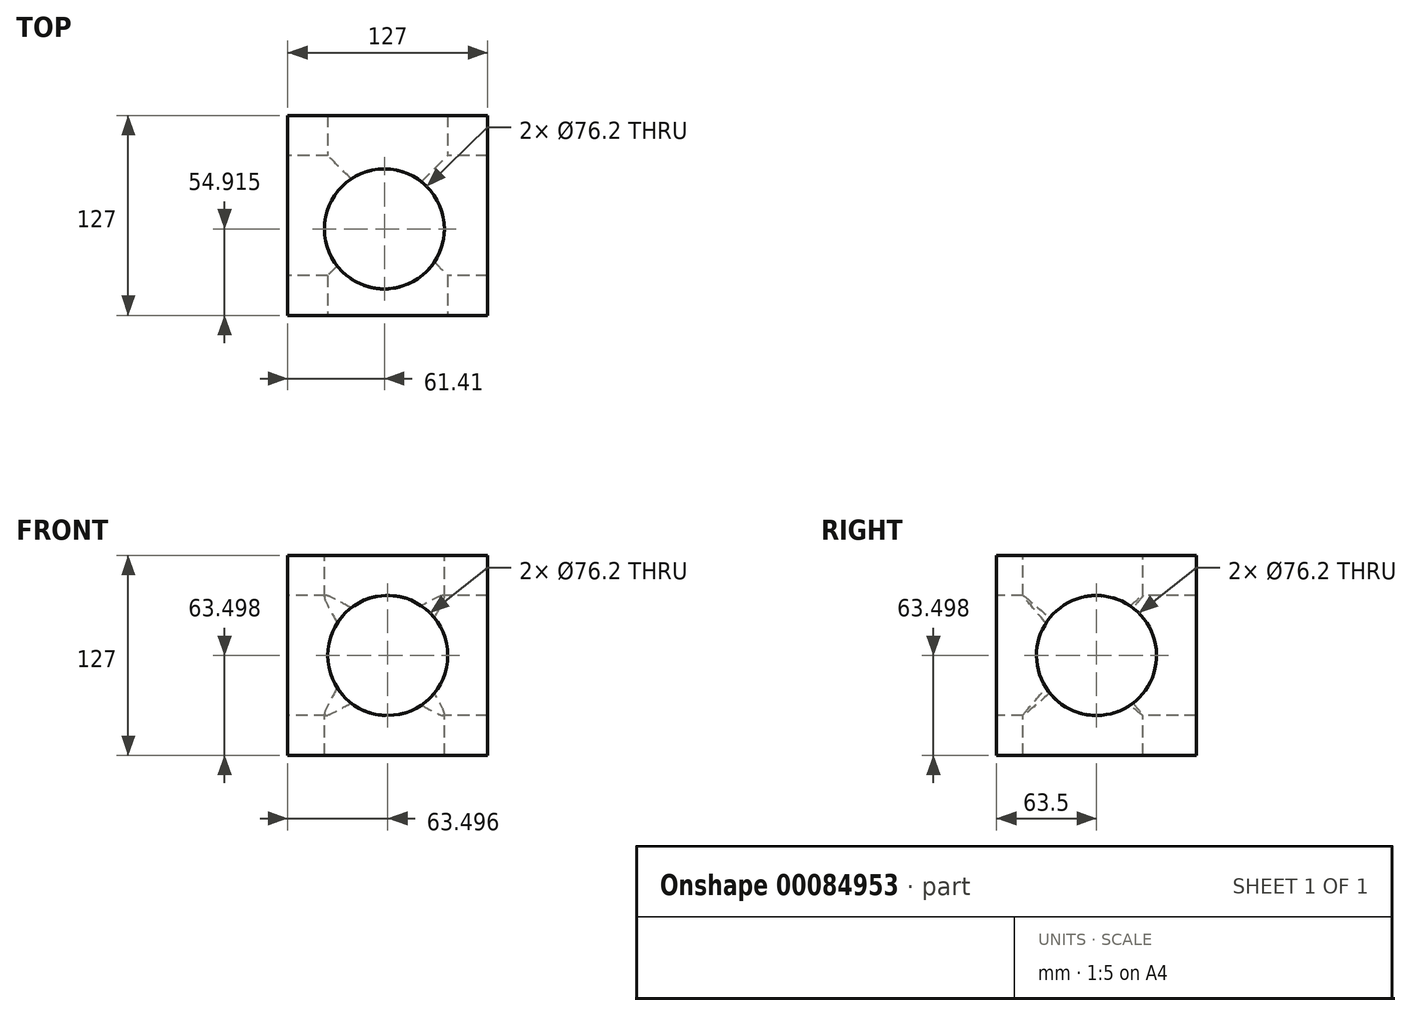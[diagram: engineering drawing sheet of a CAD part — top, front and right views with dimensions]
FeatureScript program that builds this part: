
annotation { "Feature Type Name" : "Feature", "Feature Type Description" : "" }
export const myFeature = defineFeature(function(context is Context, id is Id, definition is map)
    precondition{}
    {
        {
            var Q0;
            Q0=qCreatedBy(makeId("Front.planeOp"),FACE);
            var sketch = newSketch(context, id + "F0", { "sketchPlane" : qUnion([Q0])});
            skLineSegment(sketch, "E0.bottom", {"start": v(-61.41, 52.56) * mm, "end": v(65.59, 52.56) * mm});
            skLineSegment(sketch, "E0.top", {"start": v(-61.41, -74.44) * mm, "end": v(65.59, -74.44) * mm});
            skLineSegment(sketch, "E0.left", {"start": v(-61.41, 52.56) * mm, "end": v(-61.41, -74.44) * mm});
            skLineSegment(sketch, "E0.right", {"start": v(65.59, 52.56) * mm, "end": v(65.59, -74.44) * mm});
            skSolve(sketch);
        }
        {
            var Q0;
            Q0 = qSketchRegion(id + "F0", true);
            extrude(context, id + "F1", {"entities" : qUnion([Q0]), "depth" : 127 * mm});
        }
        {
            var Q0;
            Q0=makeQuery(id+"F1.opExtrude","CAP_FACE",FACE,{"disambiguationData":[OSD([sQuery(id+"F0.wireOp",EDGE,"E0.bottom"),sQuery(id+"F0.wireOp",EDGE,"E0.top"),sQuery(id+"F0.wireOp",EDGE,"E0.left"),sQuery(id+"F0.wireOp",EDGE,"E0.right")])],"isStart":false});
            var sketch = newSketch(context, id + "F2", { "sketchPlane" : qUnion([Q0])});
            skLineSegment(sketch, "E1", {"start": v(-61.41, 52.56) * mm, "end": v(65.59, -74.44) * mm, "construction": true});
            skCircle(sketch, "E2", {"center": v(2.09, -10.94) * mm, "radius": 38.1 * mm});
            skSolve(sketch);
        }
        {
            var Q0;
            Q0 = qSketchRegion(id + "F2", true);
            extrude(context, id + "F3", {"entities" : qUnion([Q0]), "operationType" : NewBodyOperationType.REMOVE, "endBound" : BoundingType.THROUGH_ALL, "oppositeDirection" : true, "depth" : 25.4 * mm});
        }
        {
            var Q0;
            Q0=makeQuery(id+"F1.opExtrude","SWEPT_FACE",FACE,{"disambiguationData":[OSD([sQuery(id+"F0.wireOp",EDGE,"E0.left")])]});
            var sketch = newSketch(context, id + "F4", { "sketchPlane" : qUnion([Q0])});
            skLineSegment(sketch, "E3", {"start": v(0, 52.56) * mm, "end": v(127, -74.44) * mm, "construction": true});
            skCircle(sketch, "E4", {"center": v(63.5, -10.94) * mm, "radius": 38.1 * mm});
            skSolve(sketch);
        }
        {
            var Q0;
            Q0 = qSketchRegion(id + "F4", true);
            extrude(context, id + "F5", {"entities" : qUnion([Q0]), "operationType" : NewBodyOperationType.REMOVE, "endBound" : BoundingType.THROUGH_ALL, "oppositeDirection" : true, "depth" : 25.4 * mm});
        }
        {
            var Q0;
            Q0=makeQuery(id+"F1.opExtrude","SWEPT_FACE",FACE,{"disambiguationData":[OSD([sQuery(id+"F0.wireOp",EDGE,"E0.bottom")])]});
            var sketch = newSketch(context, id + "F6", { "sketchPlane" : qUnion([Q0])});
            skLineSegment(sketch, "E5", {"start": v(-61.41, 0) * mm, "end": v(65.59, -127) * mm, "construction": true});
            skCircle(sketch, "E6", {"center": v(0, -72.08) * mm, "radius": 38.1 * mm});
            skSolve(sketch);
        }
        {
            var Q0;
            Q0 = qSketchRegion(id + "F6", true);
            extrude(context, id + "F7", {"entities" : qUnion([Q0]), "operationType" : NewBodyOperationType.REMOVE, "endBound" : BoundingType.THROUGH_ALL, "oppositeDirection" : true, "depth" : 25.4 * mm});
        }
    });
